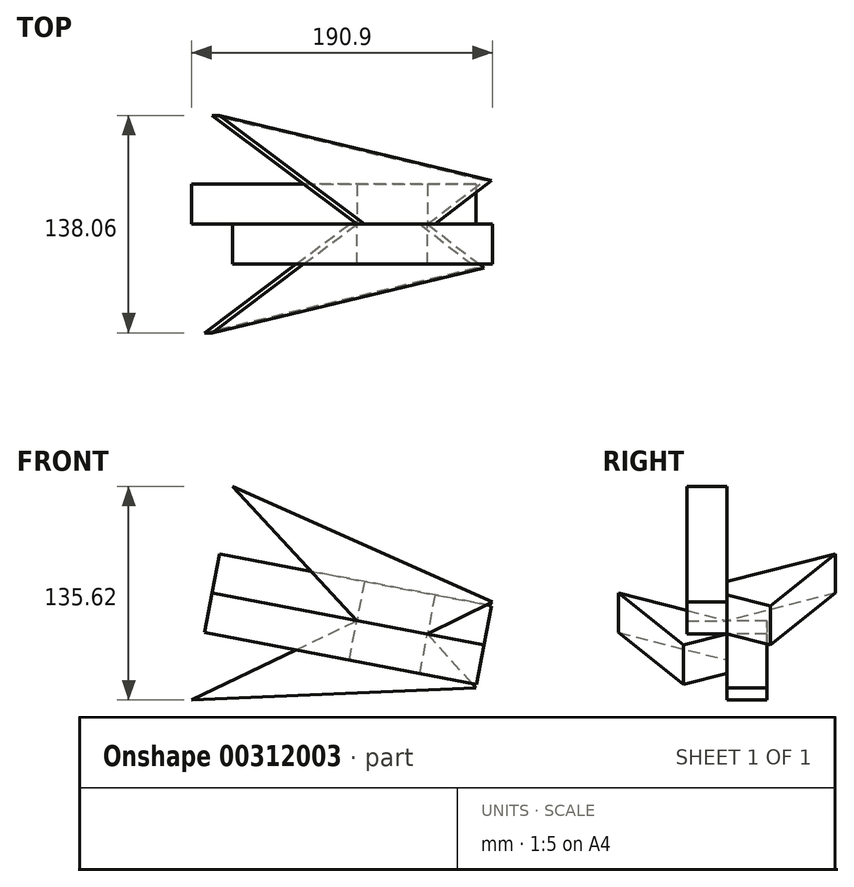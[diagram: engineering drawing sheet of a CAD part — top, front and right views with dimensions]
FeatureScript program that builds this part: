
annotation { "Feature Type Name" : "Feature", "Feature Type Description" : "" }
export const myFeature = defineFeature(function(context is Context, id is Id, definition is map)
    precondition{}
    {
        {
            var Q0;
            Q0=qCreatedBy(makeId("Front.planeOp"),FACE);
            var sketch = newSketch(context, id + "F0", { "sketchPlane" : qUnion([Q0])});
            skLineSegment(sketch, "E0", {"start": v(58.7, 60.15) * mm, "end": v(-106.38, 133.6) * mm});
            skLineSegment(sketch, "E1", {"start": v(-106.38, 133.6) * mm, "end": v(-27.38, 48.3) * mm});
            skLineSegment(sketch, "E2", {"start": v(-27.38, 48.3) * mm, "end": v(17.49, 39.76) * mm});
            skLineSegment(sketch, "E3", {"start": v(17.49, 39.76) * mm, "end": v(58.7, 60.15) * mm});
            skSolve(sketch);
        }
        {
            var Q0;
            Q0=makeQuery(id+"F0.imprint","IMPRINT",FACE,{"disambiguationData":[TD([[makeQuery(id+"F0.imprint","IMPRINT",EDGE,{"derivedFrom":sQuery(id+"F0.wireOp",EDGE,"E0")}),1.0]])]});
            extrude(context, id + "F1", {"entities" : qUnion([Q0]), "depth" : 25.4 * mm});
        }
        {
            var Q0;
            Q0=makeQuery(id+"F1.opExtrude","SWEPT_BODY",BODY,{"disambiguationData":[OSD([sQuery(id+"F0.wireOp",EDGE,"E0"),sQuery(id+"F0.wireOp",EDGE,"E1"),sQuery(id+"F0.wireOp",EDGE,"E2"),sQuery(id+"F0.wireOp",EDGE,"E3")])]});
            var Q1;
            Q1=makeQuery(id+"F1.opExtrude","CAP_EDGE",EDGE,{"disambiguationData":[OSD([sQuery(id+"F0.wireOp",EDGE,"E2")])],"isStart":true});
            circularPattern(context, id + "F2", {"entities" : qUnion([Q0]), "axis" : qUnion([Q1]), "angle" : 360 * degree, "instanceCount" : 4, "equalSpace" : true});
        }
    });
